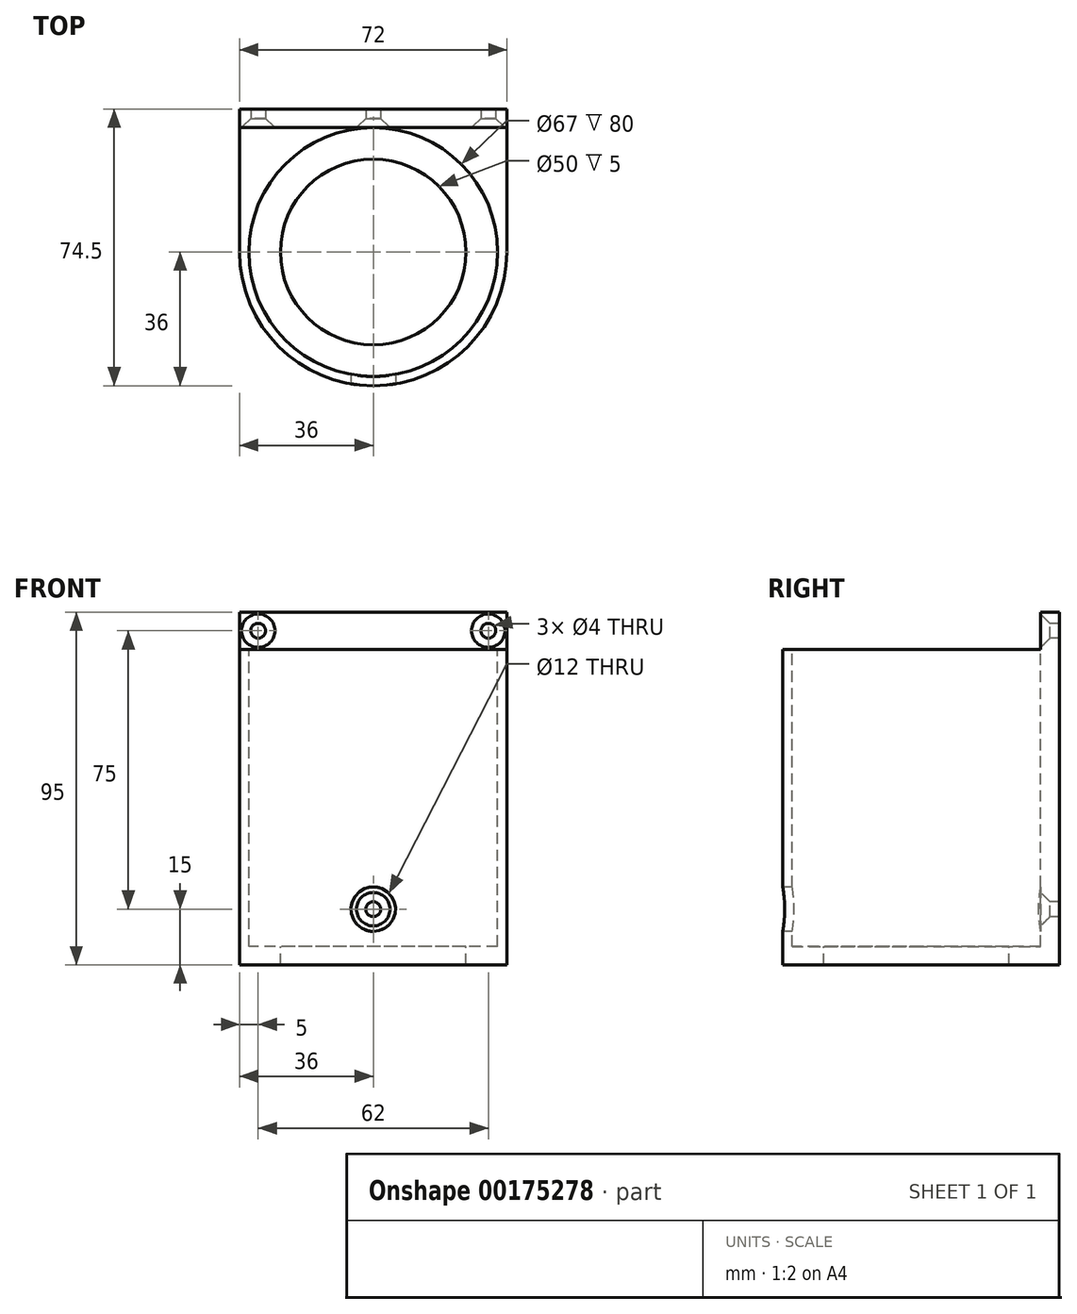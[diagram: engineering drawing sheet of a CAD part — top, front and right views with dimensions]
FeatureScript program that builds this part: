
annotation { "Feature Type Name" : "Feature", "Feature Type Description" : "" }
export const myFeature = defineFeature(function(context is Context, id is Id, definition is map)
    precondition{}
    {
        {
            var Q0;
            Q0=qCreatedBy(makeId("Top.planeOp"),FACE);
            var sketch = newSketch(context, id + "F0", { "sketchPlane" : qUnion([Q0])});
            skLineSegment(sketch, "E0", {"start": v(-36, 38.5) * mm, "end": v(36, 38.5) * mm});
            skLineSegment(sketch, "E1", {"start": v(36, 38.5) * mm, "end": v(36, 0) * mm});
            skLineSegment(sketch, "E2", {"start": v(-36, 38.5) * mm, "end": v(-36, 0) * mm});
            skArc(sketch, "E3", {"start": v(-36, 0) * mm, "mid": v(0, -36) * mm, "end": v(36, 0) * mm});
            skPoint(sketch, "E3.third.point", {"position": v(0, -36) * mm});
            skSolve(sketch);
        }
        {
            var Q0;
            Q0 = qSketchRegion(id + "F0", true);
            extrude(context, id + "F1", {"entities" : qUnion([Q0]), "depth" : 95 * mm});
        }
        {
            var Q0;
            Q0=makeQuery(id+"F1.opExtrude","CAP_FACE",FACE,{"disambiguationData":[OSD([sQuery(id+"F0.wireOp",EDGE,"E0"),sQuery(id+"F0.wireOp",EDGE,"E1"),sQuery(id+"F0.wireOp",EDGE,"E2"),sQuery(id+"F0.wireOp",EDGE,"E3")])],"isStart":false});
            var sketch = newSketch(context, id + "F2", { "sketchPlane" : qUnion([Q0])});
            skLineSegment(sketch, "E4", {"start": v(-36, 33.5) * mm, "end": v(-36, -46.5) * mm});
            skLineSegment(sketch, "E5", {"start": v(-36, -46.5) * mm, "end": v(36, -46.5) * mm});
            skLineSegment(sketch, "E6", {"start": v(36, -46.5) * mm, "end": v(36, 33.5) * mm});
            skLineSegment(sketch, "E7", {"start": v(36, 33.5) * mm, "end": v(-36, 33.5) * mm});
            skSolve(sketch);
        }
        {
            var Q0;
            Q0 = qSketchRegion(id + "F2", true);
            extrude(context, id + "F3", {"entities" : qUnion([Q0]), "operationType" : NewBodyOperationType.REMOVE, "oppositeDirection" : true, "depth" : 10 * mm});
        }
        {
            var Q0;
            Q0=makeQuery(id+"F3.boolean.opBoolean","COPY",FACE,{"derivedFrom":makeQuery(id+"F3.opExtrude","CAP_FACE",FACE,{"disambiguationData":[OSD([sQuery(id+"F2.wireOp",EDGE,"E4"),sQuery(id+"F2.wireOp",EDGE,"E5"),sQuery(id+"F2.wireOp",EDGE,"E6"),sQuery(id+"F2.wireOp",EDGE,"E7")])],"isStart":false})});
            var sketch = newSketch(context, id + "F4", { "sketchPlane" : qUnion([Q0])});
            skCircle(sketch, "E8", {"center": v(0, 0) * mm, "radius": 33.5 * mm});
            skSolve(sketch);
        }
        {
            var Q0;
            Q0 = qSketchRegion(id + "F4", true);
            extrude(context, id + "F5", {"entities" : qUnion([Q0]), "operationType" : NewBodyOperationType.REMOVE, "oppositeDirection" : true, "depth" : 80 * mm});
        }
        {
            var Q0;
            Q0=makeQuery(id+"F3.boolean.opBoolean","COPY",FACE,{"derivedFrom":makeQuery(id+"F3.opExtrude","SWEPT_FACE",FACE,{"disambiguationData":[OSD([sQuery(id+"F2.wireOp",EDGE,"E7")])]})});
            var sketch = newSketch(context, id + "F6", { "sketchPlane" : qUnion([Q0])});
            skPoint(sketch, "E9", {"position": v(-31, 90) * mm});
            skPoint(sketch, "E10", {"position": v(31, 90) * mm});
            skSolve(sketch);
        }
        {
            var Q0;
            Q0=sQuery(id+"F6.wireOp",VERTEX,"E9");
            var Q1;
            Q1=sQuery(id+"F6.wireOp",VERTEX,"E10");
            var Q2;
            Q2=makeQuery(id+"F1.opExtrude","SWEPT_BODY",BODY,{"disambiguationData":[OSD([sQuery(id+"F0.wireOp",EDGE,"E0"),sQuery(id+"F0.wireOp",EDGE,"E1"),sQuery(id+"F0.wireOp",EDGE,"E2"),sQuery(id+"F0.wireOp",EDGE,"E3")])]});
            hole(context, id + "F7", {"style" : HoleStyle.C_SINK, "endStyle" : HoleEndStyle.THROUGH, "holeDiameter" : 4 * mm, "cSinkDiameter" : 9 * mm, "cSinkAngle" : 90 * degree, "startFromSketch" : true, "locations" : qUnion([Q0, Q1]), "scope" : qUnion([Q2]), "isTappedThrough" : true});
        }
        {
            var Q0;
            Q0=makeQuery(id+"F5.boolean.opBoolean","COPY",FACE,{"derivedFrom":makeQuery(id+"F5.opExtrude","CAP_FACE",FACE,{"disambiguationData":[OSD([sQuery(id+"F4.wireOp",EDGE,"E8")])],"isStart":false})});
            var sketch = newSketch(context, id + "F8", { "sketchPlane" : qUnion([Q0])});
            skCircle(sketch, "E11", {"center": v(0, 0) * mm, "radius": 25 * mm});
            skSolve(sketch);
        }
        {
            var Q0;
            Q0 = qSketchRegion(id + "F8", true);
            extrude(context, id + "F9", {"entities" : qUnion([Q0]), "operationType" : NewBodyOperationType.REMOVE, "endBound" : BoundingType.THROUGH_ALL, "oppositeDirection" : true, "depth" : 25 * mm});
        }
        {
            var Q0;
            Q0=qCreatedBy(makeId("Front.planeOp"),FACE);
            cPlane(context, id + "F10", {"entities" : qUnion([Q0]), "cplaneType" : CPlaneType.OFFSET, "offset" : 40 * mm, "width" : 150 * mm, "height" : 150 * mm});
        }
        {
            var Q0;
            Q0=qCreatedBy(id+"F10.planeOp",FACE);
            var sketch = newSketch(context, id + "F11", { "sketchPlane" : qUnion([Q0])});
            skCircle(sketch, "E12", {"center": v(0, 15) * mm, "radius": 6 * mm});
            skSolve(sketch);
        }
        {
            var Q0;
            Q0 = qSketchRegion(id + "F11", true);
            extrude(context, id + "F12", {"entities" : qUnion([Q0]), "operationType" : NewBodyOperationType.REMOVE, "oppositeDirection" : true, "depth" : 73.5 * mm});
        }
        {
            var Q0;
            Q0=makeQuery(id+"F12.boolean.opBoolean","COPY",FACE,{"derivedFrom":makeQuery(id+"F12.opExtrude","CAP_FACE",FACE,{"disambiguationData":[OSD([sQuery(id+"F11.wireOp",EDGE,"E12")])],"isStart":false})});
            var sketch = newSketch(context, id + "F13", { "sketchPlane" : qUnion([Q0])});
            skPoint(sketch, "E13", {"position": v(0, 15) * mm});
            skSolve(sketch);
        }
        {
            var Q0;
            Q0=sQuery(id+"F13.wireOp",VERTEX,"E13");
            var Q1;
            Q1=makeQuery(id+"F1.opExtrude","SWEPT_BODY",BODY,{"disambiguationData":[OSD([sQuery(id+"F0.wireOp",EDGE,"E0"),sQuery(id+"F0.wireOp",EDGE,"E1"),sQuery(id+"F0.wireOp",EDGE,"E2"),sQuery(id+"F0.wireOp",EDGE,"E3")])]});
            hole(context, id + "F14", {"style" : HoleStyle.C_SINK, "endStyle" : HoleEndStyle.THROUGH, "holeDiameter" : 4 * mm, "cSinkDiameter" : 9 * mm, "cSinkAngle" : 90 * degree, "startFromSketch" : true, "locations" : qUnion([Q0]), "scope" : qUnion([Q1]), "isTappedThrough" : true});
        }
    });
